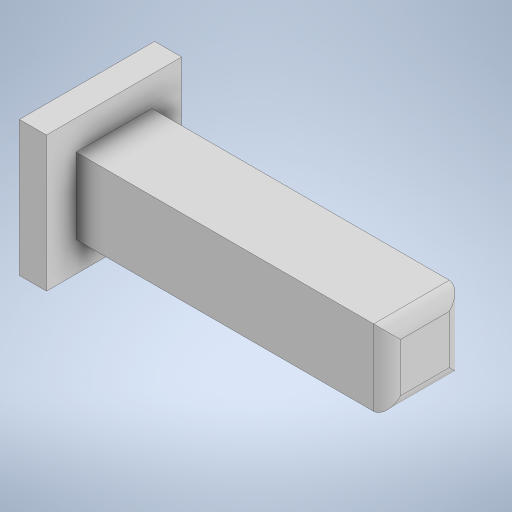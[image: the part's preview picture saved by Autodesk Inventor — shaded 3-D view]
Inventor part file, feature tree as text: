
AUTODESK INVENTOR PART (.ipt)
format: ipt  version: 2023 (Build 270158030, 158C)  size: 227,840 bytes
history: native  units: mm
features: extrude x2, sketch x2, fillet x1
ambient origin geometry x8: Origin, YZ Plane, XZ Plane, XY Plane, X Axis, Y Axis, Z Axis, Center Point
bodies: Solid1 (feature_tree)
feature tree (5):
  extrude  "Extrusion1"  Depth=5.0mm
  extrude  "Extrusion2"  Depth=2.8mm
  fillet  "Fillet1"  Radius=2.8mm
  sketch  "Sketch1"  dims[d0=5.0mm d1=5.0mm]
  sketch  "Sketch2"  dims[d2=1.0mm d3=0.0mm d4=2.8mm d5=2.8mm d6=1.1mm d7=1.1mm d8=11.5mm d9=0.0mm d10=0.5mm]
